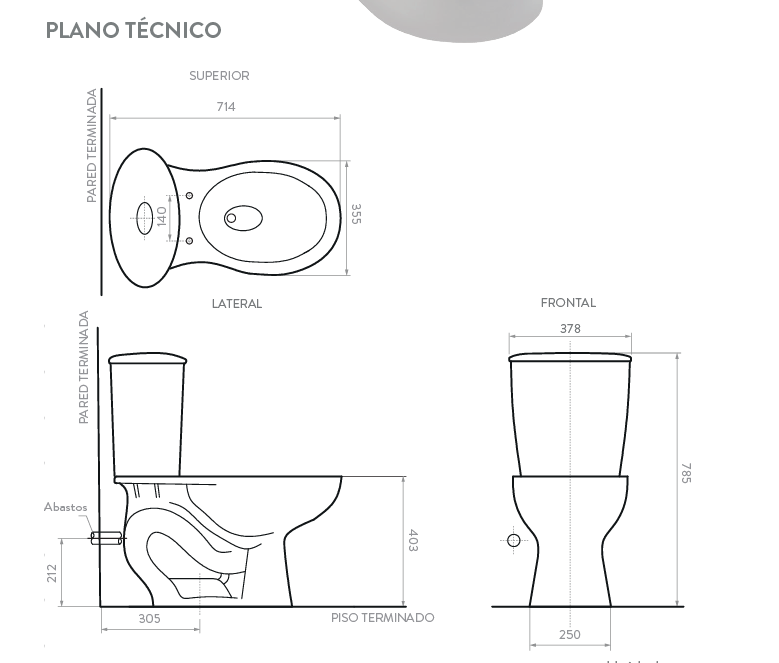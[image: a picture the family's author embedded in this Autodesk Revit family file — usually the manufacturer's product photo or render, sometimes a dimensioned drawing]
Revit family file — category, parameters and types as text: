
# Revit family: 020801001_Sanitario Powermax Blanco
name_source: partatom
category: Plumbing Fixtures
units: mm (PartAtom-declared; Revit-internal decimal feet)

## family parameters
Always vertical = Yes
Cut with Voids When Loaded = No
OmniClass Number = 23.31.19.17
OmniClass Title = Toilets With Tank
Part Type = Normal
Room Calculation Point = No
Round Connector Dimension = Use Diameter
Shared = No
Work Plane-Based = No

## types (1)
- 020801001_Sanitario Powermax Blanco
    Alto = 708 mm  [stored 2.32283 ft]
    Altura de Sello = 5.8 cm
    Altura de instalación Según Norma = 30.5 cm
    Ancho = 382 mm
    Consumo de Agua = 3.8 Lts
    Creado por = IDD
    Description = Consumo de agua promedio de 3.8 Lpf. (4.8 Lpf. para sólidos / 3.2 Lpf. para líquidos).
    Dimensiones generales producto (H * W * D) = 81.8 cmx 38.2 cmx 70.8cm
    Espejo de Agua = 174x209
    Fecha de creación = 13/08/2020
    Manufacturer = CORONA
    Material = Corona_Porcelana_Sanitaria
    Material 2 = Corona_Aluminio
    Model = Sanitario Powermax Blanco
    Peso Neto aprox = 36,804 Kg
    Presion maxima = 25 - 80 PSI
    Profundidad = 718 mm
    Sistema de Carga = Por gravedad
    Sistema de Descarga = flushmate Descarga con Presión Asistida
    URL = https://corona.co

note: [stored X ft] marks values corroborated as IEEE doubles in the binary element streams (Revit-internal decimal feet)

## geometry (parser evidence)
native form markers: Sweep x2
no freeform markers — native parametric forms only
